# Revit family: FU_Table_Sandler_Moon_8-1
name_source: partatom
category: Furniture
units: mm (PartAtom-declared; Revit-internal decimal feet)

## family parameters
Always vertical = Yes
Cut with Voids When Loaded = No
OmniClass Number = 23.40.20.00
OmniClass Title = General Furniture and Specialties
Room Calculation Point = No
Shared = No
Work Plane-Based = No

## types (1)
- Moon Table 8.1
    Base Frame Finish = Metal - Chrome - Polished
    Default Elevation = 0 mm  [stored 0 ft]
    Description = Table with four spoke steel rod frame. The table top is available in varnished oak veneer or lacquered colors. Table top size: Ø60cm.
    Manufacturer = Sandler
    Model = Moon 8.1
    Top Diameter = 600 mm
    Top Finish = Wood - Oak - Walnut
    URL = https://www.sandlerseating.com

note: [stored X ft] marks values corroborated as IEEE doubles in the binary element streams (Revit-internal decimal feet)

## geometry (parser evidence)
native form markers: Sweep x2
no freeform markers — native parametric forms only
